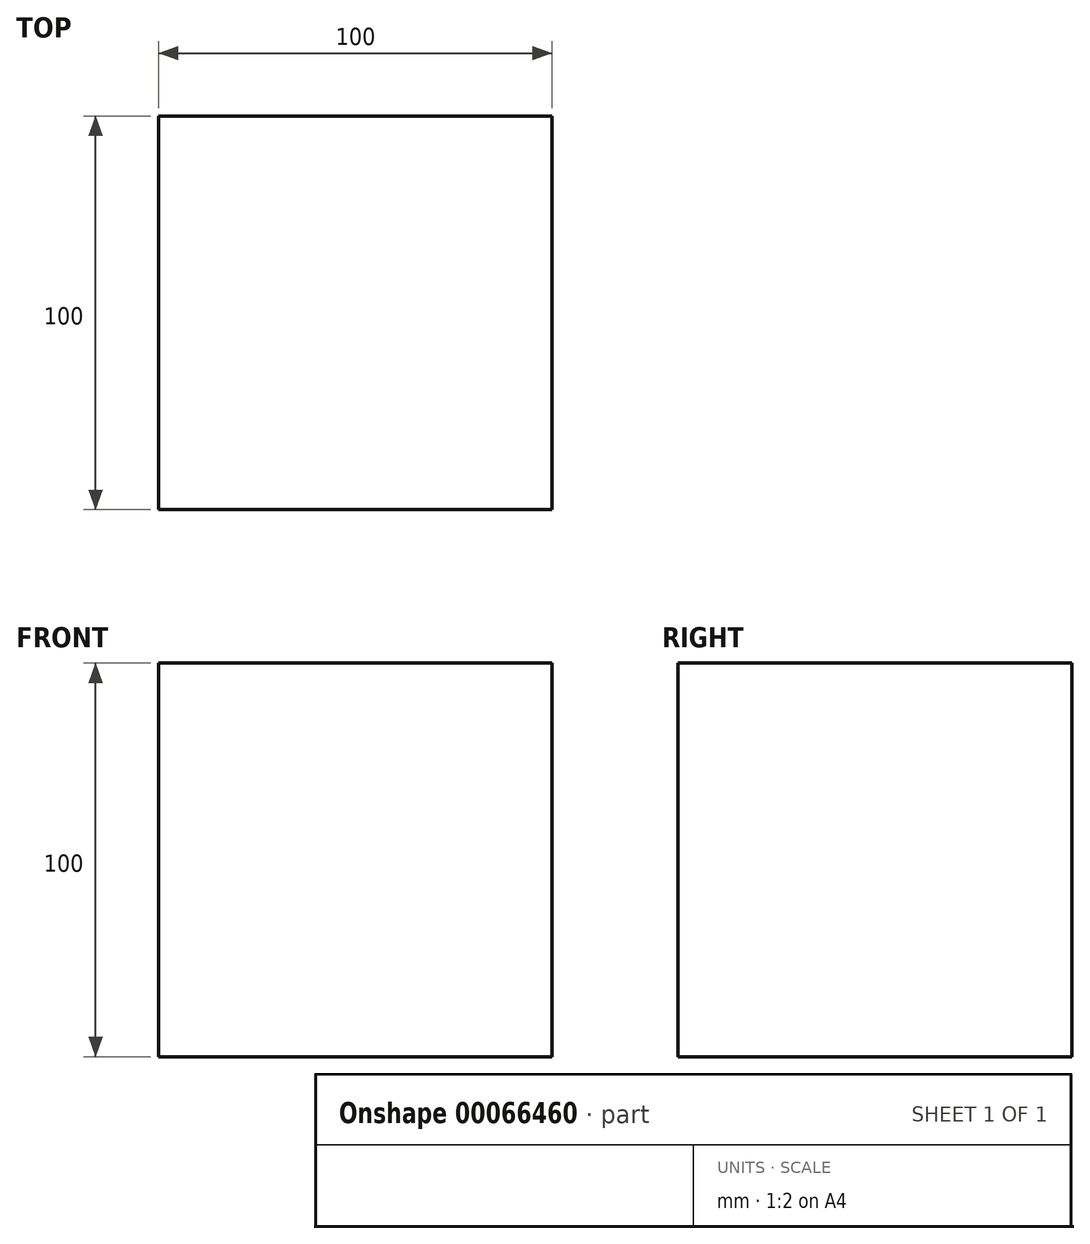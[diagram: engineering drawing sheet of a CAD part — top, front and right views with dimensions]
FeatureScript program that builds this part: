
annotation { "Feature Type Name" : "Feature", "Feature Type Description" : "" }
export const myFeature = defineFeature(function(context is Context, id is Id, definition is map)
    precondition{}
    {
        {
            var Q0;
            Q0=qCreatedBy(makeId("Front.planeOp"),FACE);
            var sketch = newSketch(context, id + "F0", { "sketchPlane" : qUnion([Q0])});
            skLineSegment(sketch, "E0.rect.bottom", {"start": v(50, 50) * mm, "end": v(-50, 50) * mm});
            skLineSegment(sketch, "E0.rect.top", {"start": v(50, -50) * mm, "end": v(-50, -50) * mm});
            skLineSegment(sketch, "E0.rect.left", {"start": v(50, 50) * mm, "end": v(50, -50) * mm});
            skLineSegment(sketch, "E0.rect.right", {"start": v(-50, 50) * mm, "end": v(-50, -50) * mm});
            skPoint(sketch, "E0.rect.middle", {"position": v(0, 0) * mm});
            skSolve(sketch);
        }
        {
            var Q0;
            Q0 = qSketchRegion(id + "F0", true);
            extrude(context, id + "F1", {"entities" : qUnion([Q0]), "endBound" : BoundingType.SYMMETRIC, "depth" : 100 * mm});
        }
    });
